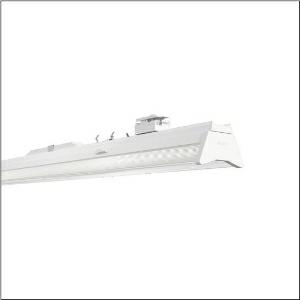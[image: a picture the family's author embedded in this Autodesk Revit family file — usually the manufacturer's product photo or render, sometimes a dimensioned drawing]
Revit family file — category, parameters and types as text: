
# Revit family: licross_r__11_performance_ho_51tm16mn4gxm_a288
name_source: partatom
category: Lighting Fixtures
units: mm (PartAtom-declared; Revit-internal decimal feet)

## family parameters
Cut with Voids When Loaded = No
Host = Face
Light Source = No
Part Type = Normal
Room Calculation Point = No
Round Connector Dimension = Use Diameter
Shared = No

## types (1)
- --- (1 x LED, 16020 lm, 87.4 W, 4000K)
    Apparent Load = 87 VA
    CIE Flux Codes = 63 87 95 78 100
    Color Rendering = 80
    Color Temperature = 4000K
    Default Elevation = 1800 mm
    Description = Licross® 11 Performance HO, luminaire insert, of sheet steel, galvanised, coil coated, white, length: 1.500mm, width: 120mm, height: 123mm, LED rated luminous flux: 16.020lm, light colour: 840, control gear: ON/OFF Multilumen, with plug, 3-pole, with phase selection, mains connection: 220..240V, AC, 50/60Hz, rated input power: 87W, halogen-free wiring, primary light control with lens, of plastic, primary optical cover: cover, of PMMA, light emission: direct/indirect distribution, primary light characteristic: symmetric, protection rating (complete): IP40, insulation class (complete): insulation class I (protective earthing), certification: CE, ENEC, VDE, UKCA, protection symbol: D if used in an environment without relevant dust loads with corresponding accessories, impact resistance: IK06, permissible ambient temperature for indoor applications: -35..+35°C, corresponds to IFS (International Featured Standards) requirements for safety and quality in the food industry, reducing of maximum allowable ambient temperature of 5°C with ceiling mounting, LABS conformity tested according to VDMA 24364:2018-05, packaging unit: 1 piece
    Height = 114 mm
    Lamp = 1 x LED
    Lamp Light Flux = 16020 lm
    Lamp Power = 87.4 W
    Lamp count = 1
    Length = 1500 mm
    Luminous efficacy = 183 lm/W
    Manufacturer = Siteco
    ModVariant = No
    Model = 51TM16MN4GXM
    Mounting Place = Ceiling
    Mounting Type = Pendant
    Number of Poles = 1
    OnlyDefault = Yes
    Power Factor = 1
    Product Name = Licross® 11 Performance HO
    Product group = luminaire insert
    ProductGroupID = 902
    Protection Class = Protection class I
    Protection Degree = IP 40
    RLX_Detail_Level = 1
    RLX_Emergency_Light_Flux = 0 lm
    RLX_Emergency_Type = 0
    RLX_Emergency_Type_DB = No
    RlxData = <blob elided: 31697 chars, md5=1b19a06c>
    Socket = socket
    Standby Power = 0 W
    System Light Flux = 16020 lm
    System Power = 87 W
    Type Comments = factory setting: luminous flux: 100 % | (A | C | E) | 203 mA
    Type Image = l_1256138.jpg
    URL = http://relux.com
    VarID = @adj_086228
    Voltage = 0 V
    Weight = 0.00 kg
    Width = 120 mm

## geometry (parser evidence)
native form markers: Blend x4, Sweep x13
no freeform markers — native parametric forms only
